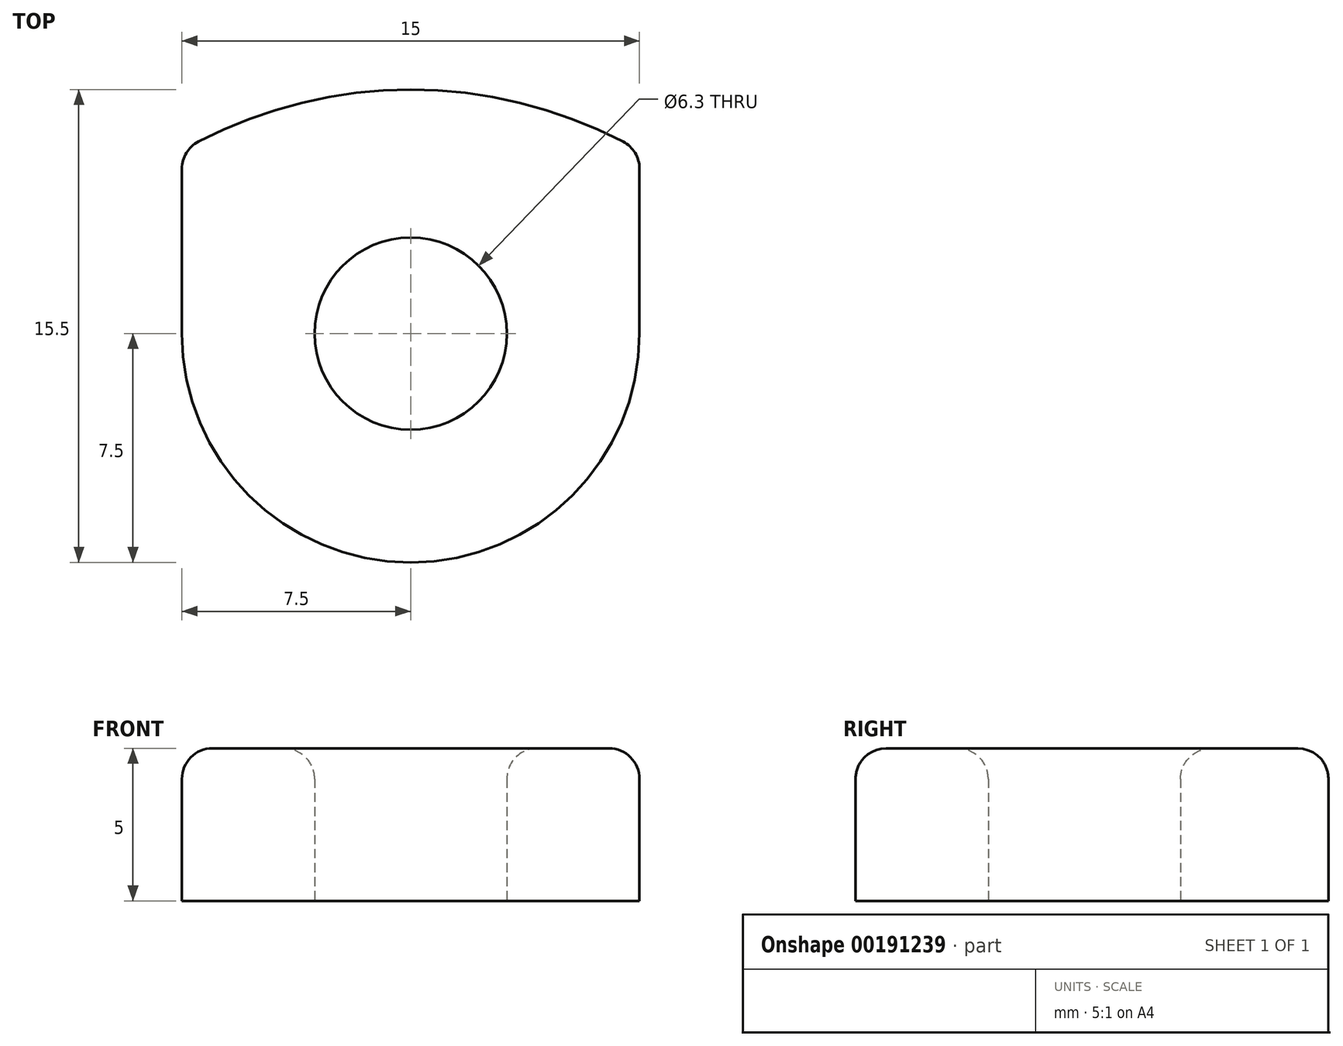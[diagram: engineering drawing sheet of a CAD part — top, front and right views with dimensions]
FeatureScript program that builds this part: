
annotation { "Feature Type Name" : "Feature", "Feature Type Description" : "" }
export const myFeature = defineFeature(function(context is Context, id is Id, definition is map)
    precondition{}
    {
        {
            var Q0;
            Q0=qCreatedBy(makeId("Top.planeOp"),FACE);
            var sketch = newSketch(context, id + "F0", { "sketchPlane" : qUnion([Q0])});
            skCircle(sketch, "E0", {"center": v(0, 0) * mm, "radius": 3.15 * mm});
            skArc(sketch, "E1", {"start": v(-7.5, 0) * mm, "mid": v(0, -7.5) * mm, "end": v(7.5, 0) * mm});
            skLineSegment(sketch, "E2", {"start": v(-7.5, 0) * mm, "end": v(-7.5, 6) * mm});
            skLineSegment(sketch, "E3", {"start": v(-7.5, 6) * mm, "end": v(7.5, 6) * mm, "construction": true});
            skLineSegment(sketch, "E4", {"start": v(7.5, 6) * mm, "end": v(7.5, 0) * mm});
            skLineSegment(sketch, "E5", {"start": v(0, 6) * mm, "end": v(0, 8) * mm, "construction": true});
            skArc(sketch, "E6", {"start": v(7.5, 6) * mm, "mid": v(0, 8) * mm, "end": v(-7.5, 6) * mm});
            skSolve(sketch);
        }
        {
            var Q0;
            Q0=makeQuery(id+"F0.imprint","IMPRINT",FACE,{"disambiguationData":[TD([[makeQuery(id+"F0.imprint","IMPRINT",EDGE,{"derivedFrom":sQuery(id+"F0.wireOp",EDGE,"E0")}),-1.0]])]});
            extrude(context, id + "F1", {"entities" : qUnion([Q0]), "depth" : 5 * mm});
        }
        {
            var Q0;
            Q0=makeQuery(id+"F1.opExtrude","SWEPT_EDGE",EDGE,{"disambiguationData":[OSD([sQuery(id+"F0.wireOp",EDGE,"E2"),sQuery(id+"F0.wireOp",EDGE,"E6")])]});
            var Q1;
            Q1=makeQuery(id+"F1.opExtrude","SWEPT_EDGE",EDGE,{"disambiguationData":[OSD([sQuery(id+"F0.wireOp",EDGE,"E4"),sQuery(id+"F0.wireOp",EDGE,"E6")])]});
            fillet(context, id + "F2", {"entities" : qUnion([Q0, Q1]), "radius" : 1 * mm, "tangentPropagation" : true, "allowEdgeOverflow" : false});
        }
        {
            var Q0;
            Q0=makeQuery(id+"F1.opExtrude","CAP_EDGE",EDGE,{"disambiguationData":[OSD([sQuery(id+"F0.wireOp",EDGE,"E2")])],"isStart":false});
            var Q1;
            Q1=makeQuery(id+"F1.opExtrude","CAP_EDGE",EDGE,{"disambiguationData":[OSD([sQuery(id+"F0.wireOp",EDGE,"E0")])],"isStart":false});
            fillet(context, id + "F3", {"entities" : qUnion([Q0, Q1]), "radius" : 1 * mm, "tangentPropagation" : true, "allowEdgeOverflow" : false});
        }
    });
